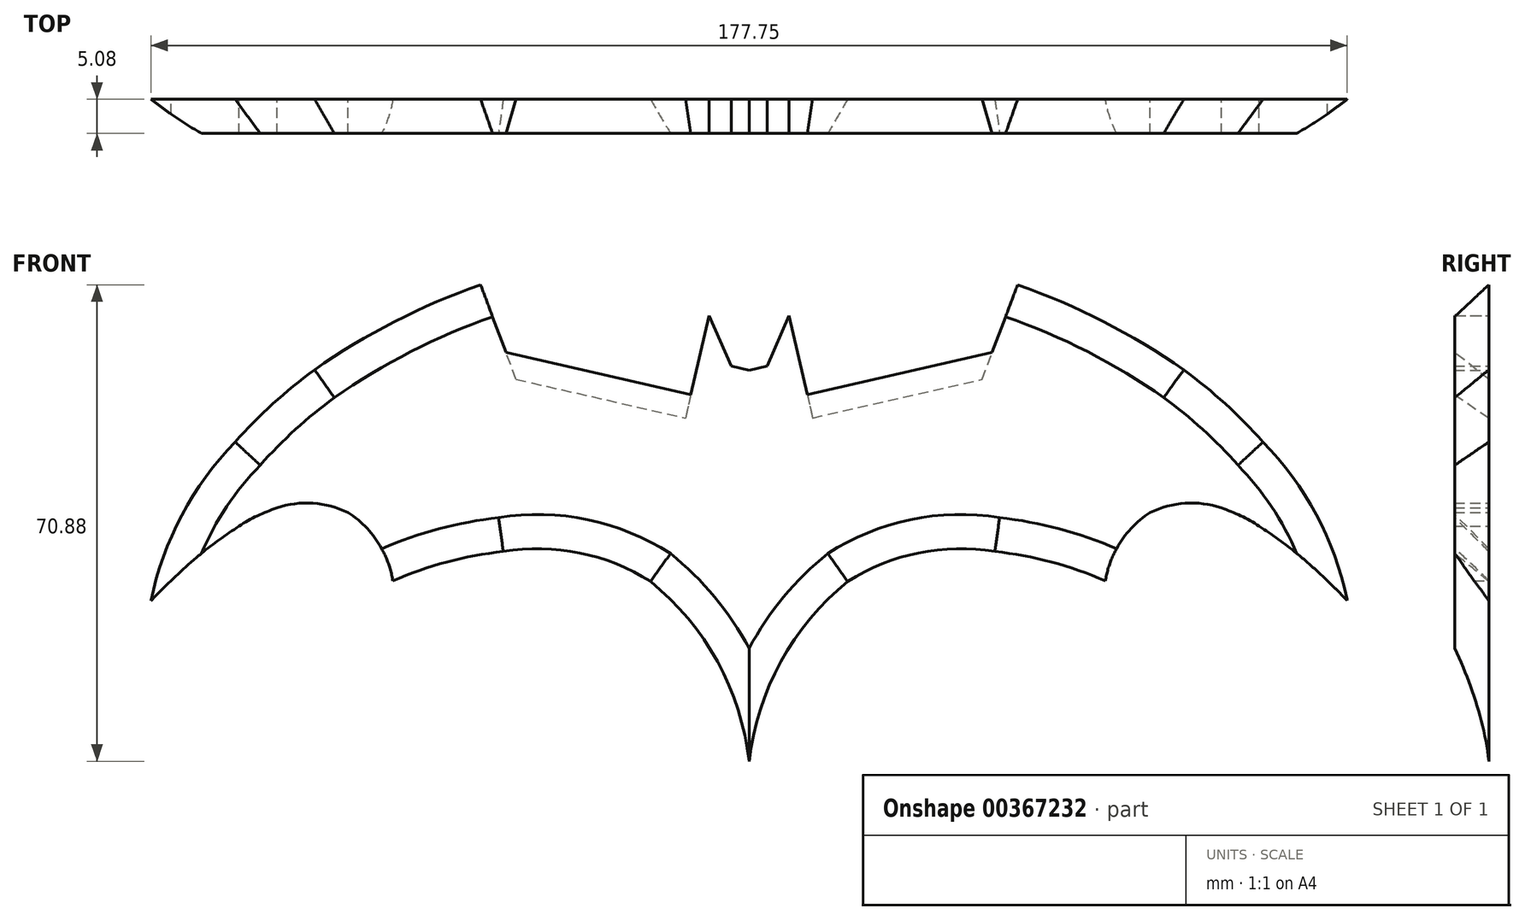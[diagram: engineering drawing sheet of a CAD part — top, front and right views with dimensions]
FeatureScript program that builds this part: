
annotation { "Feature Type Name" : "Feature", "Feature Type Description" : "" }
export const myFeature = defineFeature(function(context is Context, id is Id, definition is map)
    precondition{}
    {
        {
            var Q0;
            Q0=qCreatedBy(makeId("Front.planeOp"),FACE);
            var sketch = newSketch(context, id + "F0", { "sketchPlane" : qUnion([Q0])});
            skLineSegment(sketch, "E0", {"start": v(0, 27.26) * mm, "end": v(-2.66, 27.87) * mm});
            skLineSegment(sketch, "E1", {"start": v(-2.66, 27.87) * mm, "end": v(-5.95, 35.4) * mm});
            skLineSegment(sketch, "E2", {"start": v(-5.95, 35.4) * mm, "end": v(-8.65, 23.64) * mm});
            skLineSegment(sketch, "E3", {"start": v(-8.65, 23.64) * mm, "end": v(-36.12, 29.9) * mm});
            skLineSegment(sketch, "E4", {"start": v(-36.12, 29.9) * mm, "end": v(-39.9, 39.98) * mm});
            skLineSegment(sketch, "E5.MirrorCS", {"start": v(0, 27.26) * mm, "end": v(2.66, 27.87) * mm});
            skLineSegment(sketch, "E6.MirrorCS", {"start": v(2.66, 27.87) * mm, "end": v(5.95, 35.4) * mm});
            skLineSegment(sketch, "E7.MirrorCS", {"start": v(5.95, 35.4) * mm, "end": v(8.65, 23.64) * mm});
            skLineSegment(sketch, "E8.MirrorCS", {"start": v(8.65, 23.64) * mm, "end": v(36.12, 29.9) * mm});
            skLineSegment(sketch, "E9.MirrorCS", {"start": v(36.12, 29.9) * mm, "end": v(39.9, 39.98) * mm});
            skArc(sketch, "E10", {"start": v(-39.9, 39.98) * mm, "mid": v(-52.68, 34.5) * mm, "end": v(-64.58, 27.32) * mm});
            skArc(sketch, "E11", {"start": v(-64.58, 27.32) * mm, "mid": v(-70.76, 22.27) * mm, "end": v(-76.37, 16.6) * mm});
            skArc(sketch, "E12", {"start": v(-76.37, 16.6) * mm, "mid": v(-84.32, 5.68) * mm, "end": v(-88.9, -7.02) * mm});
            skArc(sketch, "E13", {"start": v(-85.91, -4.05) * mm, "mid": v(-87.44, -5.5) * mm, "end": v(-88.9, -7.02) * mm});
            skArc(sketch, "E14", {"start": v(-75.8, 4.07) * mm, "mid": v(-81.07, 0.28) * mm, "end": v(-85.91, -4.05) * mm});
            skArc(sketch, "E15", {"start": v(-70.16, 6.78) * mm, "mid": v(-73.07, 5.61) * mm, "end": v(-75.8, 4.07) * mm});
            skArc(sketch, "E16", {"start": v(-59.6, 6.1) * mm, "mid": v(-64.81, 7.5) * mm, "end": v(-70.16, 6.78) * mm});
            skArc(sketch, "E17", {"start": v(-52.94, -4.07) * mm, "mid": v(-55.19, 1.72) * mm, "end": v(-59.6, 6.1) * mm});
            skArc(sketch, "E18", {"start": v(-36.53, 0.31) * mm, "mid": v(-44.9, -1.26) * mm, "end": v(-52.94, -4.07) * mm});
            skArc(sketch, "E19", {"start": v(-14.66, -4.14) * mm, "mid": v(-25.18, 0.1) * mm, "end": v(-36.53, 0.31) * mm});
            skArc(sketch, "E20", {"start": v(0, -30.9) * mm, "mid": v(-4.7, -16.08) * mm, "end": v(-14.66, -4.14) * mm});
            skArc(sketch, "E21.MirrorCS", {"start": v(0, -30.9) * mm, "mid": v(4.7, -16.08) * mm, "end": v(14.66, -4.14) * mm});
            skArc(sketch, "E22.MirrorCS", {"start": v(14.66, -4.14) * mm, "mid": v(25.18, 0.1) * mm, "end": v(36.53, 0.31) * mm});
            skArc(sketch, "E23.MirrorCS", {"start": v(36.53, 0.31) * mm, "mid": v(44.9, -1.26) * mm, "end": v(52.94, -4.07) * mm});
            skArc(sketch, "E24.MirrorCS", {"start": v(52.94, -4.07) * mm, "mid": v(55.19, 1.72) * mm, "end": v(59.6, 6.1) * mm});
            skArc(sketch, "E25.MirrorCS", {"start": v(59.6, 6.1) * mm, "mid": v(64.81, 7.5) * mm, "end": v(70.16, 6.78) * mm});
            skArc(sketch, "E26.MirrorCS", {"start": v(70.16, 6.78) * mm, "mid": v(73.07, 5.61) * mm, "end": v(75.8, 4.07) * mm});
            skArc(sketch, "E27.MirrorCS", {"start": v(75.8, 4.07) * mm, "mid": v(81.07, 0.28) * mm, "end": v(85.91, -4.05) * mm});
            skArc(sketch, "E28.MirrorCS", {"start": v(85.91, -4.05) * mm, "mid": v(87.44, -5.5) * mm, "end": v(88.9, -7.02) * mm});
            skArc(sketch, "E29.MirrorCS", {"start": v(76.37, 16.6) * mm, "mid": v(84.32, 5.68) * mm, "end": v(88.9, -7.02) * mm});
            skArc(sketch, "E30.MirrorCS", {"start": v(64.58, 27.32) * mm, "mid": v(70.76, 22.27) * mm, "end": v(76.37, 16.6) * mm});
            skArc(sketch, "E31.MirrorCS", {"start": v(39.9, 39.98) * mm, "mid": v(52.68, 34.5) * mm, "end": v(64.58, 27.32) * mm});
            skLineSegment(sketch, "E32", {"start": v(-88.95, 40.99) * mm, "end": v(-88.95, -30.9) * mm});
            skLineSegment(sketch, "E33", {"start": v(88.85, 40.99) * mm, "end": v(88.85, -30.9) * mm});
            skPoint(sketch, "E34.orphan", {"position": v(88.85, -31.91) * mm});
            skPoint(sketch, "E35.orphan", {"position": v(-88.95, -31.91) * mm});
            skLineSegment(sketch, "E36", {"start": v(-88.95, -30.9) * mm, "end": v(88.85, -30.9) * mm});
            skLineSegment(sketch, "E37", {"start": v(-88.95, 39.98) * mm, "end": v(88.85, 39.98) * mm});
            skSolve(sketch);
        }
        {
            var Q0;
            {var subQ2=sQuery(id+"F0.wireOp",EDGE,"E0");Q0=makeQuery(id+"F0.imprint","IMPRINT",FACE,{"disambiguationData":[TD([[makeQuery(id+"F0.imprint","IMPRINT",EDGE,{"derivedFrom":subQ2}),1.0]])]});}
            var Q1;
            {var subQ1=sQuery(id+"F0.wireOp",EDGE,"E5.MirrorCS");Q1=makeQuery(id+"F0.imprint","IMPRINT",FACE,{"disambiguationData":[TD([[makeQuery(id+"F0.imprint","IMPRINT",EDGE,{"derivedFrom":subQ1}),-1.0]])]});}
            extrude(context, id + "F1", {"entities" : qUnion([Q0, Q1]), "endBound" : BoundingType.SYMMETRIC, "depth" : 5.08 * mm});
        }
        {
            var Q0;
            Q0=makeQuery(id+"F1.opExtrude","CAP_EDGE",EDGE,{"disambiguationData":[OSD([sQuery(id+"F0.wireOp",EDGE,"E10")])],"isStart":false});
            var Q1;
            Q1=makeQuery(id+"F1.opExtrude","CAP_EDGE",EDGE,{"disambiguationData":[OSD([sQuery(id+"F0.wireOp",EDGE,"E12")])],"isStart":false});
            var Q2;
            Q2=makeQuery(id+"F1.opExtrude","CAP_EDGE",EDGE,{"disambiguationData":[OSD([sQuery(id+"F0.wireOp",EDGE,"E31.MirrorCS")])],"isStart":false});
            var Q3;
            Q3=makeQuery(id+"F1.opExtrude","CAP_EDGE",EDGE,{"disambiguationData":[OSD([sQuery(id+"F0.wireOp",EDGE,"E29.MirrorCS")])],"isStart":false});
            var Q4;
            Q4=makeQuery(id+"F1.opExtrude","CAP_EDGE",EDGE,{"disambiguationData":[OSD([sQuery(id+"F0.wireOp",EDGE,"E30.MirrorCS")])],"isStart":false});
            var Q5;
            Q5=makeQuery(id+"F1.opExtrude","CAP_EDGE",EDGE,{"disambiguationData":[OSD([sQuery(id+"F0.wireOp",EDGE,"E11")])],"isStart":false});
            chamfer(context, id + "F2", {"entities" : qUnion([Q0, Q1, Q2, Q3, Q4, Q5]), "width" : 5.08 * mm, "tangentPropagation" : true});
        }
        {
            var Q0;
            Q0=makeQuery(id+"F1.opExtrude","CAP_EDGE",EDGE,{"disambiguationData":[OSD([sQuery(id+"F0.wireOp",EDGE,"E20")])],"isStart":false});
            var Q1;
            Q1=makeQuery(id+"F1.opExtrude","CAP_EDGE",EDGE,{"disambiguationData":[OSD([sQuery(id+"F0.wireOp",EDGE,"E21.MirrorCS")])],"isStart":false});
            var Q2;
            Q2=makeQuery(id+"F1.opExtrude","CAP_EDGE",EDGE,{"disambiguationData":[OSD([sQuery(id+"F0.wireOp",EDGE,"E19")])],"isStart":false});
            var Q3;
            Q3=makeQuery(id+"F1.opExtrude","CAP_EDGE",EDGE,{"disambiguationData":[OSD([sQuery(id+"F0.wireOp",EDGE,"E22.MirrorCS")])],"isStart":false});
            var Q4;
            Q4=makeQuery(id+"F1.opExtrude","CAP_EDGE",EDGE,{"disambiguationData":[OSD([sQuery(id+"F0.wireOp",EDGE,"E18")])],"isStart":false});
            var Q5;
            Q5=makeQuery(id+"F1.opExtrude","CAP_EDGE",EDGE,{"disambiguationData":[OSD([sQuery(id+"F0.wireOp",EDGE,"E23.MirrorCS")])],"isStart":false});
            chamfer(context, id + "F3", {"entities" : qUnion([Q0, Q1, Q2, Q3, Q4, Q5]), "width" : 5.08 * mm, "tangentPropagation" : true});
        }
        {
            var Q0;
            Q0=makeQuery(id+"F1.opExtrude","CAP_EDGE",EDGE,{"disambiguationData":[OSD([sQuery(id+"F0.wireOp",EDGE,"E3")])],"isStart":true});
            var Q1;
            Q1=makeQuery(id+"F1.opExtrude","CAP_EDGE",EDGE,{"disambiguationData":[OSD([sQuery(id+"F0.wireOp",EDGE,"E8.MirrorCS")])],"isStart":true});
            chamfer(context, id + "F4", {"entities" : qUnion([Q0, Q1]), "chamferType" : ChamferType.OFFSET_ANGLE, "width" : 5.08 * mm, "oppositeDirection" : false, "angle" : 35 * degree, "tangentPropagation" : true});
        }
    });
